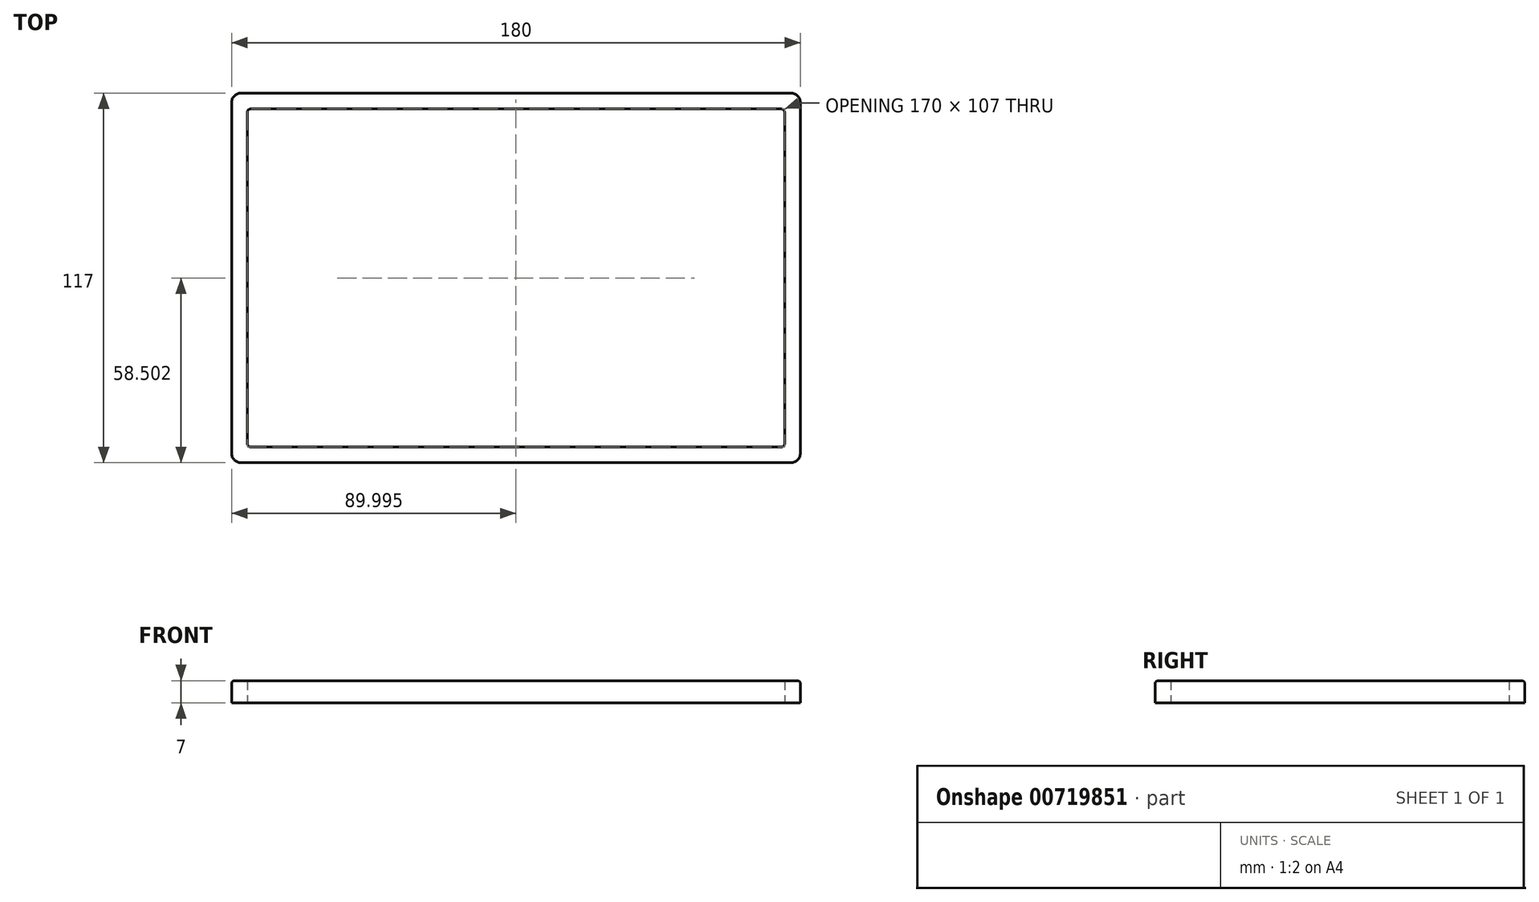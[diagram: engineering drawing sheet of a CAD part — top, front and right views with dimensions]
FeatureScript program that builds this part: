
annotation { "Feature Type Name" : "Feature", "Feature Type Description" : "" }
export const myFeature = defineFeature(function(context is Context, id is Id, definition is map)
    precondition{}
    {
        {
            var Q0;
            Q0=qCreatedBy(makeId("Top.planeOp"),FACE);
            var sketch = newSketch(context, id + "F0", { "sketchPlane" : qUnion([Q0])});
            skLineSegment(sketch, "E0.bottom", {"start": v(-119.74, 85.66) * mm, "end": v(60.26, 85.66) * mm});
            skLineSegment(sketch, "E0.top", {"start": v(-119.74, -31.34) * mm, "end": v(60.26, -31.34) * mm});
            skLineSegment(sketch, "E0.left", {"start": v(-119.74, 85.66) * mm, "end": v(-119.74, -31.34) * mm});
            skLineSegment(sketch, "E0.right", {"start": v(60.26, 85.66) * mm, "end": v(60.26, -31.34) * mm});
            skPoint(sketch, "E0.middle", {"position": v(-29.74, 27.16) * mm});
            skSolve(sketch);
        }
        {
            var Q0;
            Q0=makeQuery(id+"F0.imprint","IMPRINT",FACE,{"disambiguationData":[TD([[makeQuery(id+"F0.imprint","IMPRINT",EDGE,{"derivedFrom":sQuery(id+"F0.wireOp",EDGE,"E0.bottom")}),-1.0]])]});
            var sketch = newSketch(context, id + "F1", { "sketchPlane" : qUnion([Q0])});
            skLineSegment(sketch, "E1.bottom", {"start": v(55.26, -26.34) * mm, "end": v(-114.74, -26.34) * mm});
            skLineSegment(sketch, "E1.top", {"start": v(55.26, 80.66) * mm, "end": v(-114.74, 80.66) * mm});
            skLineSegment(sketch, "E1.left", {"start": v(55.26, -26.34) * mm, "end": v(55.26, 80.66) * mm});
            skLineSegment(sketch, "E1.right", {"start": v(-114.74, -26.34) * mm, "end": v(-114.74, 80.66) * mm});
            skPoint(sketch, "E1.middle", {"position": v(-29.74, 27.16) * mm});
            skSolve(sketch);
        }
        {
            var Q0;
            Q0 = qSketchRegion(id + "F0", true);
            extrude(context, id + "F2", {"entities" : qUnion([Q0]), "depth" : 7 * mm, "offsetDistance" : 25 * mm});
        }
        {
            var Q0;
            Q0=makeQuery(id+"F1.imprint","IMPRINT",FACE,{"disambiguationData":[TD([[makeQuery(id+"F1.imprint","IMPRINT",EDGE,{"derivedFrom":sQuery(id+"F1.wireOp",EDGE,"E1.bottom")}),-1.0]])]});
            extrude(context, id + "F3", {"entities" : qUnion([Q0]), "operationType" : NewBodyOperationType.REMOVE, "depth" : 25 * mm, "offsetDistance" : 25 * mm});
        }
        {
            var Q0;
            Q0=makeQuery(id+"F2.opExtrude","SWEPT_EDGE",EDGE,{"disambiguationData":[OSD([sQuery(id+"F0.wireOp",EDGE,"E0.bottom"),sQuery(id+"F0.wireOp",EDGE,"E0.right")])]});
            var Q1;
            Q1=makeQuery(id+"F2.opExtrude","SWEPT_EDGE",EDGE,{"disambiguationData":[OSD([sQuery(id+"F0.wireOp",EDGE,"E0.top"),sQuery(id+"F0.wireOp",EDGE,"E0.right")])]});
            var Q2;
            Q2=makeQuery(id+"F2.opExtrude","SWEPT_EDGE",EDGE,{"disambiguationData":[OSD([sQuery(id+"F0.wireOp",EDGE,"E0.top"),sQuery(id+"F0.wireOp",EDGE,"E0.left")])]});
            var Q3;
            Q3=makeQuery(id+"F2.opExtrude","SWEPT_EDGE",EDGE,{"disambiguationData":[OSD([sQuery(id+"F0.wireOp",EDGE,"E0.bottom"),sQuery(id+"F0.wireOp",EDGE,"E0.left")])]});
            fillet(context, id + "F4", {"entities" : qUnion([Q0, Q1, Q2, Q3]), "radius" : 3 * mm, "tangentPropagation" : true, "allowEdgeOverflow" : false});
        }
        {
            var Q0;
            Q0=makeQuery(id+"F2.opExtrude","CAP_EDGE",EDGE,{"disambiguationData":[OSD([sQuery(id+"F0.wireOp",EDGE,"E0.left")])],"isStart":false});
            var Q1;
            Q1=makeQuery(id+"F2.opExtrude","CAP_EDGE",EDGE,{"disambiguationData":[OSD([sQuery(id+"F0.wireOp",EDGE,"E0.top")])],"isStart":false});
            var Q2;
            {var subQ0=sQuery(id+"F0.wireOp",EDGE,"E0.left");var subQ1=sQuery(id+"F0.wireOp",EDGE,"E0.top");Q2=makeQuery(id+"F4.opFillet","BLEND_EDGE",EDGE,{"blendedFrom":[makeQuery(id+"F2.opExtrude","SWEPT_EDGE",EDGE,{"disambiguationData":[OSD([subQ1,subQ0])]}),makeQuery(id+"F2.opExtrude","CAP_FACE",FACE,{"disambiguationData":[OSD([sQuery(id+"F0.wireOp",EDGE,"E0.bottom"),subQ1,subQ0,sQuery(id+"F0.wireOp",EDGE,"E0.right")])],"isStart":false})],"blendedInto":[makeQuery(id+"F2.opExtrude","CAP_FACE",FACE,{"disambiguationData":[OSD([sQuery(id+"F0.wireOp",EDGE,"E0.bottom"),subQ1,subQ0,sQuery(id+"F0.wireOp",EDGE,"E0.right")])],"isStart":false})]});}
            fillet(context, id + "F5", {"entities" : qUnion([Q0, Q1, Q2]), "radius" : 1 * mm, "tangentPropagation" : true, "allowEdgeOverflow" : false});
        }
        {
            var Q0;
            Q0=makeQuery(id+"F3.boolean.opBoolean","COPY",EDGE,{"derivedFrom":makeQuery(id+"F3.opExtrude","SWEPT_EDGE",EDGE,{"disambiguationData":[OSD([sQuery(id+"F1.wireOp",EDGE,"E1.bottom"),sQuery(id+"F1.wireOp",EDGE,"E1.left")])]})});
            var Q1;
            Q1=makeQuery(id+"F3.boolean.opBoolean","COPY",EDGE,{"derivedFrom":makeQuery(id+"F3.opExtrude","SWEPT_EDGE",EDGE,{"disambiguationData":[OSD([sQuery(id+"F1.wireOp",EDGE,"E1.top"),sQuery(id+"F1.wireOp",EDGE,"E1.left")])]})});
            var Q2;
            Q2=makeQuery(id+"F3.boolean.opBoolean","COPY",EDGE,{"derivedFrom":makeQuery(id+"F3.opExtrude","SWEPT_EDGE",EDGE,{"disambiguationData":[OSD([sQuery(id+"F1.wireOp",EDGE,"E1.top"),sQuery(id+"F1.wireOp",EDGE,"E1.right")])]})});
            var Q3;
            Q3=makeQuery(id+"F3.boolean.opBoolean","COPY",EDGE,{"derivedFrom":makeQuery(id+"F3.opExtrude","SWEPT_EDGE",EDGE,{"disambiguationData":[OSD([sQuery(id+"F1.wireOp",EDGE,"E1.bottom"),sQuery(id+"F1.wireOp",EDGE,"E1.right")])]})});
            fillet(context, id + "F6", {"entities" : qUnion([Q0, Q1, Q2, Q3]), "radius" : 1 * mm, "allowEdgeOverflow" : false});
        }
    });
